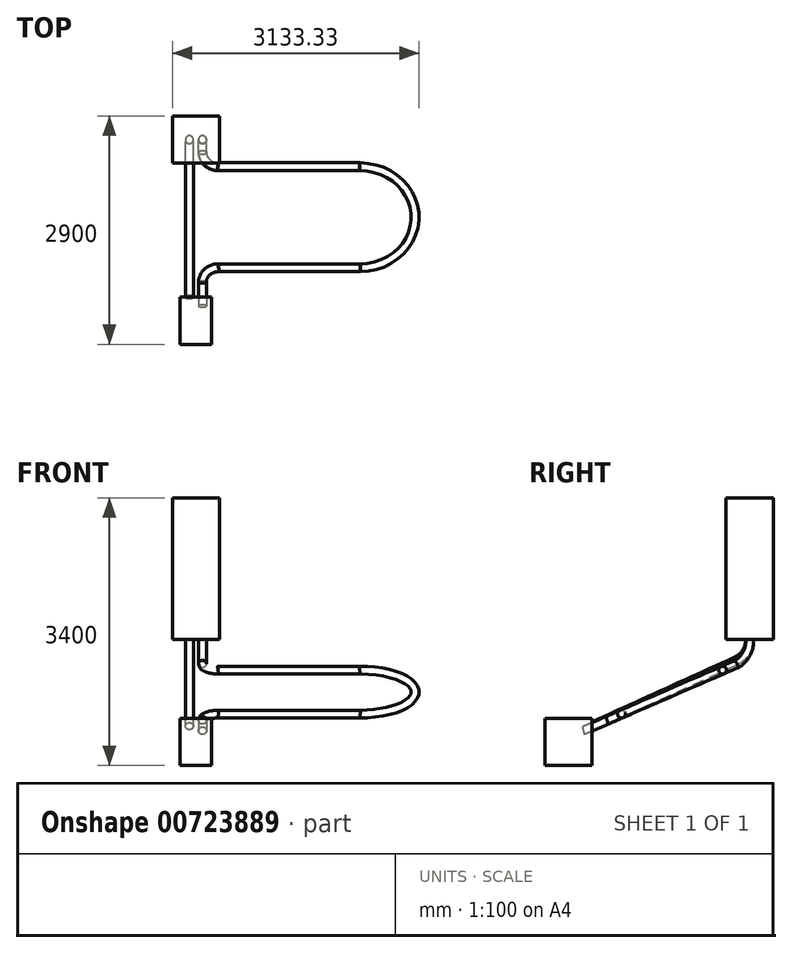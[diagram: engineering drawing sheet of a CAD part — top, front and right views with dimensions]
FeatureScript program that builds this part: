
annotation { "Feature Type Name" : "Feature", "Feature Type Description" : "" }
export const myFeature = defineFeature(function(context is Context, id is Id, definition is map)
    precondition{}
    {
        {
            assignVariable(context, id + "F0", {"name" : "PitWidth", "anyValue" : 400});
        }
        {
            assignVariable(context, id + "F1", {"name" : "PitHeight", "anyValue" : 600});
        }
        {
            var Q0;
            Q0=qCreatedBy(makeId("Top.planeOp"),FACE);
            var sketch = newSketch(context, id + "F2", { "sketchPlane" : qUnion([Q0])});
            skLineSegment(sketch, "E0.bottom", {"start": v(200, -300) * mm, "end": v(-200, -300) * mm});
            skLineSegment(sketch, "E0.top", {"start": v(200, 300) * mm, "end": v(-200, 300) * mm});
            skLineSegment(sketch, "E0.left", {"start": v(200, -300) * mm, "end": v(200, 300) * mm});
            skLineSegment(sketch, "E0.right", {"start": v(-200, -300) * mm, "end": v(-200, 300) * mm});
            skPoint(sketch, "E0.middle", {"position": v(0, 0) * mm});
            skSolve(sketch);
        }
        {
            var Q0;
            Q0 = qSketchRegion(id + "F2", true);
            extrude(context, id + "F3", {"entities" : qUnion([Q0]), "depth" : (getVariable(context, 'PitHeight')) * mm, "offsetDistance" : 25 * mm});
        }
        {
            assignVariable(context, id + "F4", {"name" : "Dist", "anyValue" : 2000});
        }
        {
            var Q0;
            Q0=qCreatedBy(makeId("Front.planeOp"),FACE);
            cPlane(context, id + "F5", {"entities" : qUnion([Q0]), "cplaneType" : CPlaneType.OFFSET, "offset" : (getVariable(context, 'Dist')) * mm, "oppositeDirection" : true, "width" : 150 * mm, "height" : 150 * mm});
        }
        {
            assignVariable(context, id + "F6", {"name" : "CabDepth", "anyValue" : 600});
        }
        {
            var Q0;
            Q0=qCreatedBy(id+"F5.planeOp",FACE);
            var sketch = newSketch(context, id + "F7", { "sketchPlane" : qUnion([Q0])});
            skLineSegment(sketch, "E1.bottom", {"start": v(300, 1600) * mm, "end": v(-300, 1600) * mm});
            skLineSegment(sketch, "E1.top", {"start": v(300, 3400) * mm, "end": v(-300, 3400) * mm});
            skLineSegment(sketch, "E1.left", {"start": v(300, 1600) * mm, "end": v(300, 3400) * mm});
            skLineSegment(sketch, "E1.right", {"start": v(-300, 1600) * mm, "end": v(-300, 3400) * mm});
            skPoint(sketch, "E1.middle", {"position": v(0, 2500) * mm});
            skSolve(sketch);
        }
        {
            var Q0;
            Q0 = qSketchRegion(id + "F7", true);
            extrude(context, id + "F8", {"entities" : qUnion([Q0]), "oppositeDirection" : true, "depth" : (getVariable(context, 'CabDepth')) * mm, "offsetDistance" : 25 * mm});
        }
        {
            assignVariable(context, id + "F9", {"name" : "PipeDia", "anyValue" : 100});
        }
        {
            assignVariable(context, id + "F10", {"name" : "PipeOffset", "anyValue" : (getVariable(context, 'PitWidth') - 2 * getVariable(context, 'PipeDia')) / 3 / 2 + getVariable(context, 'PipeDia') / 2});
        }
        {
            var Q0;
            Q0=qCreatedBy(makeId("Right.planeOp"),FACE);
            cPlane(context, id + "F11", {"entities" : qUnion([Q0]), "cplaneType" : CPlaneType.OFFSET, "offset" : (getVariable(context, 'PipeOffset')) * mm, "oppositeDirection" : true, "width" : 150 * mm, "height" : 150 * mm});
        }
        {
            var Q0;
            Q0=qCreatedBy(id+"F11.planeOp",FACE);
            var sketch = newSketch(context, id + "F12", { "sketchPlane" : qUnion([Q0])});
            skArc(sketch, "E2", {"start": v(2123.86, 1326.76) * mm, "mid": v(2252.15, 1437.45) * mm, "end": v(2300, 1600) * mm});
            skLineSegment(sketch, "E3", {"start": v(300, 500) * mm, "end": v(2123.86, 1326.76) * mm});
            skSolve(sketch);
        }
        {
            var Q0;
            Q0=sQuery(id+"F12.wireOp",VERTEX,"E3.start");
            var Q1;
            Q1=sQuery(id+"F12.wireOp",EDGE,"E3");
            cPlane(context, id + "F13", {"entities" : qUnion([Q0, Q1]), "cplaneType" : CPlaneType.LINE_POINT, "offset" : 25 * mm, "width" : 150 * mm, "height" : 150 * mm});
        }
        {
            var Q0;
            Q0=qCreatedBy(id+"F13.planeOp",FACE);
            var sketch = newSketch(context, id + "F14", { "sketchPlane" : qUnion([Q0])});
            skCircle(sketch, "E4", {"center": v(83.33, 331.54) * mm, "radius": 50 * mm});
            skSolve(sketch);
        }
        {
            var Q0;
            Q0=makeQuery(id+"F14.imprint","IMPRINT",FACE,{"disambiguationData":[TD([[makeQuery(id+"F14.imprint","IMPRINT",EDGE,{"derivedFrom":sQuery(id+"F14.wireOp",EDGE,"E4")}),1.0]])]});
            var Q1;
            Q1=sQuery(id+"F12.wireOp",EDGE,"E3");
            var Q2;
            Q2=sQuery(id+"F12.wireOp",EDGE,"E2");
            sweep(context, id + "F15", {"profiles" : qUnion([Q0]), "path" : qUnion([Q1, Q2])});
        }
        {
            var Q0;
            Q0=makeQuery(id+"F3.opExtrude","CAP_VERTEX",VERTEX,{"disambiguationData":[OSD([sQuery(id+"F2.wireOp",EDGE,"E0.top"),sQuery(id+"F2.wireOp",EDGE,"E0.right")])],"isStart":false});
            var Q1;
            Q1=makeQuery(id+"F3.opExtrude","CAP_VERTEX",VERTEX,{"disambiguationData":[OSD([sQuery(id+"F2.wireOp",EDGE,"E0.top"),sQuery(id+"F2.wireOp",EDGE,"E0.left")])],"isStart":false});
            var Q2;
            Q2=makeQuery(id+"F8.opExtrude","CAP_VERTEX",VERTEX,{"disambiguationData":[OSD([sQuery(id+"F7.wireOp",EDGE,"E1.bottom"),sQuery(id+"F7.wireOp",EDGE,"E1.left")])],"isStart":false});
            cPlane(context, id + "F16", {"entities" : qUnion([Q0, Q1, Q2]), "cplaneType" : CPlaneType.THREE_POINT, "offset" : 25 * mm, "width" : 150 * mm, "height" : 150 * mm});
        }
        {
            var Q0;
            Q0=qCreatedBy(id+"F16.planeOp",FACE);
            cPlane(context, id + "F17", {"entities" : qUnion([Q0]), "cplaneType" : CPlaneType.OFFSET, "offset" : 100 * mm, "width" : 150 * mm, "height" : 150 * mm});
        }
        {
            var Q0;
            Q0=qCreatedBy(id+"F17.planeOp",FACE);
            var sketch = newSketch(context, id + "F18", { "sketchPlane" : qUnion([Q0])});
            skLineSegment(sketch, "E5", {"start": v(283.33, -876.74) * mm, "end": v(2083.33, -876.74) * mm});
            skLineSegment(sketch, "E6", {"start": v(2083.33, -2276.74) * mm, "end": v(283.33, -2276.74) * mm});
            skArc(sketch, "E7", {"start": v(2083.33, -2276.74) * mm, "mid": v(2783.33, -1576.74) * mm, "end": v(2083.33, -876.74) * mm});
            skArc(sketch, "E8", {"start": v(83.33, -676.74) * mm, "mid": v(141.91, -818.16) * mm, "end": v(283.33, -876.74) * mm});
            skArc(sketch, "E9", {"start": v(283.33, -2276.74) * mm, "mid": v(141.91, -2335.32) * mm, "end": v(83.33, -2476.74) * mm});
            skLineSegment(sketch, "E10", {"start": v(83.33, -676.74) * mm, "end": v(83.33, -347.69) * mm});
            skLineSegment(sketch, "E11", {"start": v(83.33, -2476.74) * mm, "end": v(83.33, -3206.79) * mm, "construction": true});
            skEllipse(sketch, "E12.0", {"center": v(-83.33, -2476.74) * mm, "majorRadius": 50 * mm, "minorRadius": 5.3 * mm, "majorAxis": v(-1, 0), "construction": true});
            skSolve(sketch);
        }
        {
            var Q0;
            Q0=qCreatedBy(makeId("Right.planeOp"),FACE);
            cPlane(context, id + "F19", {"entities" : qUnion([Q0]), "cplaneType" : CPlaneType.OFFSET, "offset" : (getVariable(context, 'PipeOffset')) * mm, "width" : 150 * mm, "height" : 150 * mm});
        }
        {
            var Q0;
            Q0=qCreatedBy(id+"F19.planeOp",FACE);
            var sketch = newSketch(context, id + "F20", { "sketchPlane" : qUnion([Q0])});
            skLineSegment(sketch, "E13", {"start": v(2300, 1600) * mm, "end": v(2300, 1718.55) * mm, "construction": true});
            skLineSegment(sketch, "E14.0", {"start": v(1956.1, 1211) * mm, "end": v(2139.52, 1290.75) * mm, "construction": true});
            skLineSegment(sketch, "E15", {"start": v(2139.52, 1290.75) * mm, "end": v(1973.83, 1671.83) * mm, "construction": true});
            skArc(sketch, "E16", {"start": v(2139.52, 1290.75) * mm, "mid": v(2262.26, 1423.32) * mm, "end": v(2300, 1600) * mm});
            skSolve(sketch);
        }
        {
            var Q0;
            Q0=sQuery(id+"F18.wireOp",EDGE,"E9");
            var Q1;
            Q1=sQuery(id+"F18.wireOp",VERTEX,"E9.end");
            cPlane(context, id + "F21", {"entities" : qUnion([Q0, Q1]), "cplaneType" : CPlaneType.CURVE_POINT, "offset" : 25 * mm, "width" : 150 * mm, "height" : 150 * mm});
        }
        {
            var Q0;
            Q0=qCreatedBy(id+"F21.planeOp",FACE);
            var sketch = newSketch(context, id + "F22", { "sketchPlane" : qUnion([Q0])});
            skCircle(sketch, "E17", {"center": v(-83.33, 330.62) * mm, "radius": 50 * mm});
            skSolve(sketch);
        }
        {
            var Q0;
            Q0=makeQuery(id+"F22.imprint","IMPRINT",FACE,{"disambiguationData":[TD([[makeQuery(id+"F22.imprint","IMPRINT",EDGE,{"derivedFrom":sQuery(id+"F22.wireOp",EDGE,"E17")}),1.0]])]});
            var Q1;
            Q1=sQuery(id+"F20.wireOp",EDGE,"E16");
            var Q2;
            Q2=sQuery(id+"F18.wireOp",EDGE,"E9");
            var Q3;
            Q3=sQuery(id+"F18.wireOp",EDGE,"E6");
            var Q4;
            Q4=sQuery(id+"F18.wireOp",EDGE,"E7");
            var Q5;
            Q5=sQuery(id+"F18.wireOp",EDGE,"E5");
            var Q6;
            Q6=sQuery(id+"F18.wireOp",EDGE,"E8");
            var Q7;
            Q7=sQuery(id+"F18.wireOp",EDGE,"E10");
            sweep(context, id + "F23", {"profiles" : qUnion([Q0]), "path" : qUnion([Q1, Q2, Q3, Q4, Q5, Q6, Q7])});
        }
    });
